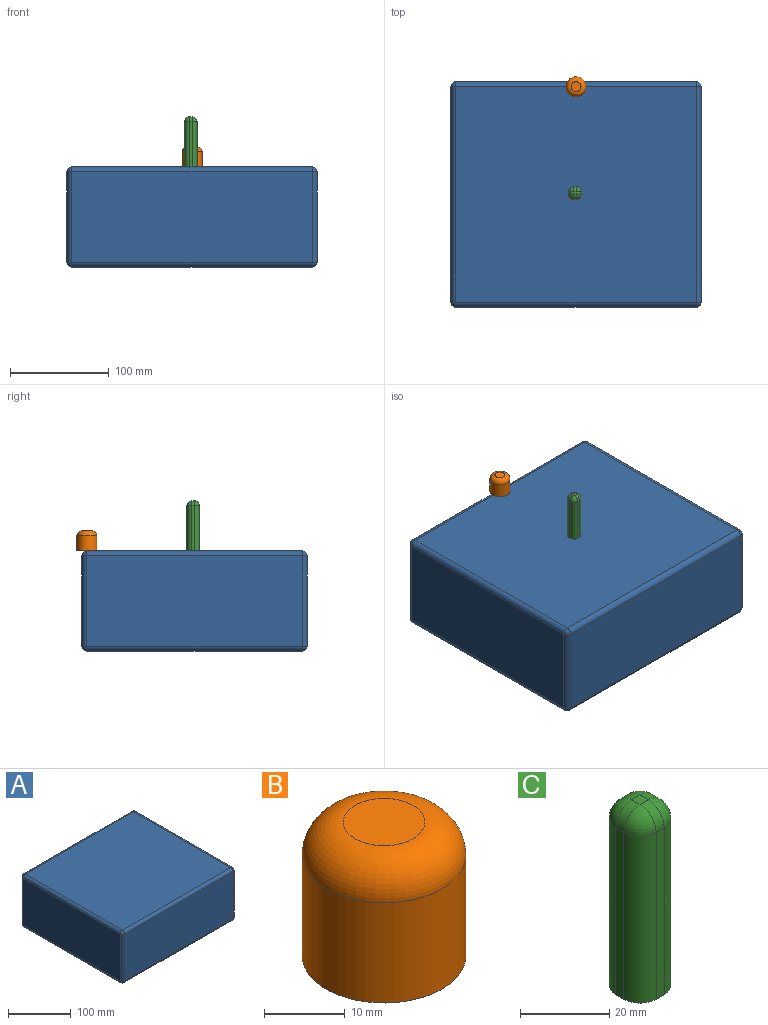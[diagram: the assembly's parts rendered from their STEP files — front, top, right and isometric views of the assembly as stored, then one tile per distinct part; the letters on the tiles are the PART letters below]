
ASSEMBLY  parts=3 mates=2
PART A: 26 faces, bbox 254x228.6x101.6 mm
  f0: plane 243.84x218.44mm, normal (0,0,1), area 53264.4mm2, adj f14,f19,f22,f25
  f1: plane 218.44x91.44mm, normal (-1,0,0), area 19974.2mm2, adj f11,f20,f21,f25
  f2: plane 243.84x218.44mm, normal (0,0,-1), area 53264.4mm2, adj f6,f10,f11,f12
  f3: plane 218.44x91.44mm, normal (1,0,0), area 19974.2mm2, adj f6,f9,f13,f14
  f4: plane 243.84x91.44mm, normal (0,-1,0), area 22296.7mm2, adj f9,f10,f19,f20
  f5: plane 243.84x91.44mm, normal (0,1,0), area 22296.7mm2, adj f12,f13,f21,f22
  f6: cylinder r=5.08mm len=218.44mm, axis (0,-1,0), area 1743.1mm2, adj f2,f3,f7,f8
  f7: sphere r=5.08mm, area 40.5mm2, adj f6,f9,f10
  f8: sphere r=5.08mm, area 40.5mm2, adj f6,f12,f13
  f9: cylinder r=5.08mm len=91.44mm, axis (0,0,-1), area 729.7mm2, adj f3,f4,f7,f15
  f10: cylinder r=5.08mm len=243.84mm, axis (-1,0,0), area 1945.8mm2, adj f2,f4,f7,f16
  f11: cylinder r=5.08mm len=218.44mm, axis (0,1,0), area 1743.1mm2, adj f1,f2,f16,f17
  f12: cylinder r=5.08mm len=243.84mm, axis (1,0,0), area 1945.8mm2, adj f2,f5,f8,f17
  f13: cylinder r=5.08mm len=91.44mm, axis (0,0,1), area 729.7mm2, adj f3,f5,f8,f18
  f14: cylinder r=5.08mm len=218.44mm, axis (0,1,0), area 1743.1mm2, adj f0,f3,f15,f18
  f15: sphere r=5.08mm, area 40.5mm2, adj f9,f14,f19
  f16: sphere r=5.08mm, area 40.5mm2, adj f10,f11,f20
  f17: sphere r=5.08mm, area 40.5mm2, adj f11,f12,f21
  f18: sphere r=5.08mm, area 40.5mm2, adj f13,f14,f22
  f19: cylinder r=5.08mm len=243.84mm, axis (1,0,0), area 1945.8mm2, adj f0,f4,f15,f23
  f20: cylinder r=5.08mm len=91.44mm, axis (0,0,1), area 729.7mm2, adj f1,f4,f16,f23
  f21: cylinder r=5.08mm len=91.44mm, axis (0,0,-1), area 729.7mm2, adj f1,f5,f17,f24
  f22: cylinder r=5.08mm len=243.84mm, axis (-1,0,0), area 1945.8mm2, adj f0,f5,f18,f24
  f23: sphere r=5.08mm, area 40.5mm2, adj f19,f20,f25
  f24: sphere r=5.08mm, area 40.5mm2, adj f21,f22,f25
  f25: cylinder r=5.08mm len=218.44mm, axis (0,-1,0), area 1743.1mm2, adj f0,f1,f23,f24
PART B: 4 faces, bbox 22x22x20.3 mm
  f0: cylinder r=10.16mm len=20.32mm, axis (0,0,-1), area 972.9mm2, adj f2,f3
  f1: plane 10.16x10.16mm, normal (0,0,1), area 81.1mm2, adj f3
  f2: plane 20.32x20.32mm, normal (0,0,-1), area 324.3mm2, adj f0
  f3: torus R=5.08mm, axis (0,0,1), area 416.8mm2, adj f0,f1
PART C: 18 faces, bbox 12.7x12.7x50.8 mm
  f0: plane 2.54x2.54mm, normal (0,0,1), area 6.5mm2, adj f8,f11,f14,f17
  f1: plane 45.72x2.54mm, normal (-1,0,0), area 116.1mm2, adj f2,f12,f13,f17
  f2: plane 12.7x12.7mm, normal (0,0,-1), area 139.1mm2, adj f1,f3,f4,f5,f6,f7,f12,f13
  f3: plane 45.72x2.54mm, normal (1,0,0), area 116.1mm2, adj f2,f6,f7,f8
  f4: plane 45.72x2.54mm, normal (0,-1,0), area 116.1mm2, adj f2,f6,f11,f12
  f5: plane 45.72x2.54mm, normal (0,1,0), area 116.1mm2, adj f2,f7,f13,f14
  f6: cylinder r=5.08mm len=45.72mm, axis (0,0,-1), area 364.8mm2, adj f2,f3,f4,f9
  f7: cylinder r=5.08mm len=45.72mm, axis (0,0,1), area 364.8mm2, adj f2,f3,f5,f10
  f8: cylinder r=5.08mm len=5.08mm, axis (0,1,0), area 20.3mm2, adj f0,f3,f9,f10
  f9: sphere r=5.08mm, area 40.5mm2, adj f6,f8,f11
  f10: sphere r=5.08mm, area 40.5mm2, adj f7,f8,f14
  f11: cylinder r=5.08mm len=5.08mm, axis (1,0,0), area 20.3mm2, adj f0,f4,f9,f15
  f12: cylinder r=5.08mm len=45.72mm, axis (0,0,1), area 364.8mm2, adj f1,f2,f4,f15
  f13: cylinder r=5.08mm len=45.72mm, axis (0,0,-1), area 364.8mm2, adj f1,f2,f5,f16
  f14: cylinder r=5.08mm len=5.08mm, axis (-1,0,0), area 20.3mm2, adj f0,f5,f10,f16
  f15: sphere r=5.08mm, area 40.5mm2, adj f11,f12,f17
  f16: sphere r=5.08mm, area 40.5mm2, adj f13,f14,f17
  f17: cylinder r=5.08mm len=5.08mm, axis (0,-1,0), area 20.3mm2, adj f0,f1,f15,f16
PLACE A t=(48.59,31.67,5.42)mm
PLACE B t=(48.59,26.59,56.22)mm
PLACE C t=(47.32,-75.01,81.62)mm
MATE fastened C.f6 <-> A.f0  axis (0,0,-1) through (48.59,-82.63,56.22)mm
MATE fastened B.f0 <-> A.f0  axis (0,0,-1) through (48.59,26.59,56.22)mm
